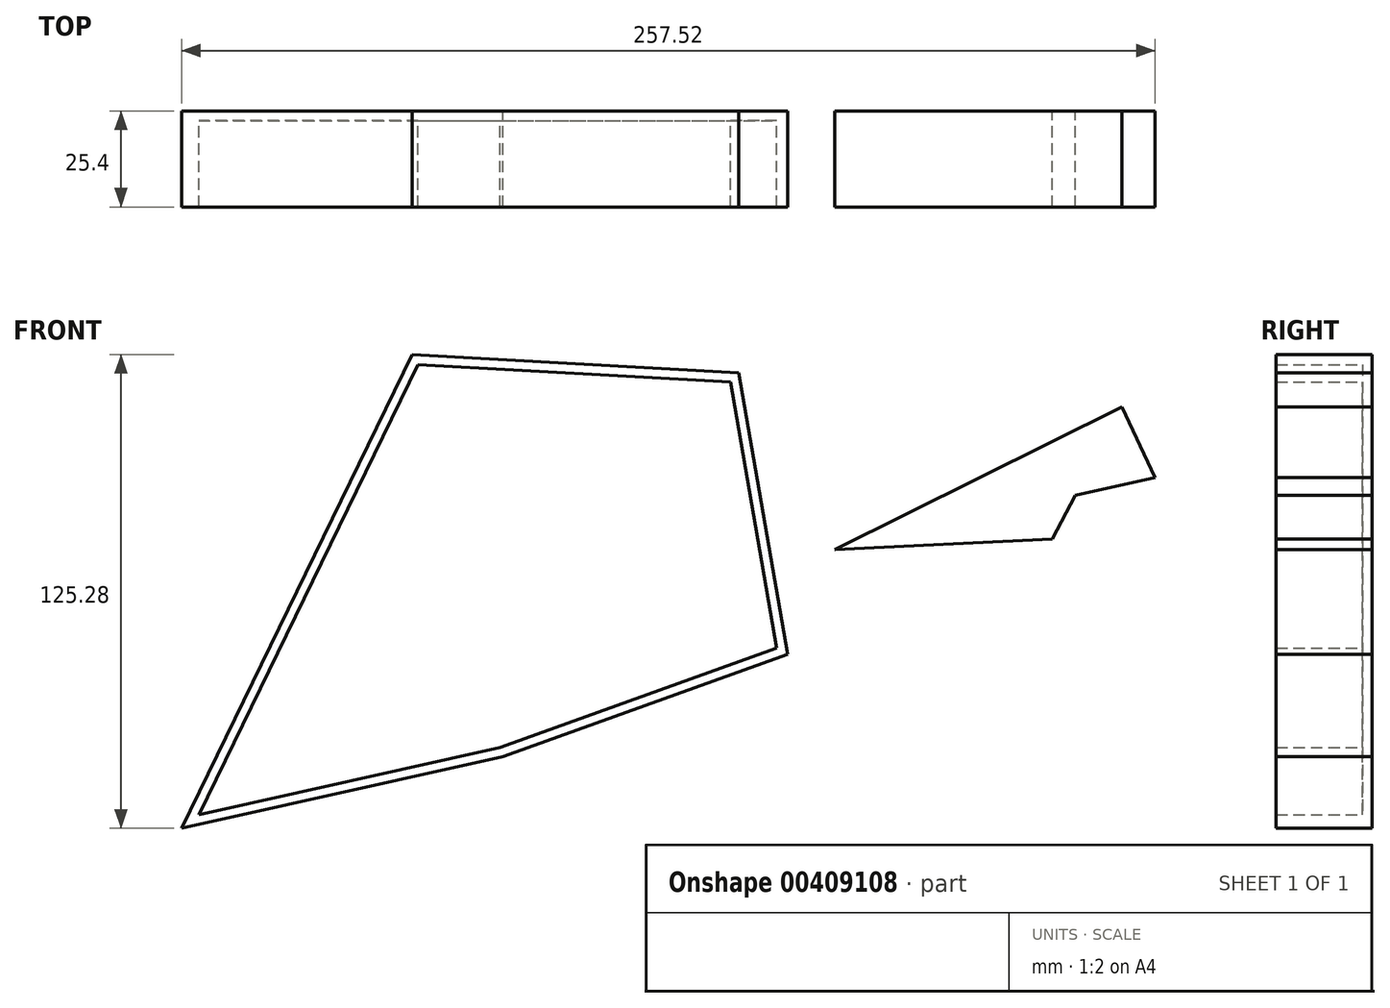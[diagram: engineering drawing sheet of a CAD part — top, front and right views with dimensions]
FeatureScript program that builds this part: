
annotation { "Feature Type Name" : "Feature", "Feature Type Description" : "" }
export const myFeature = defineFeature(function(context is Context, id is Id, definition is map)
    precondition{}
    {
        {
            var Q0;
            Q0=qCreatedBy(makeId("Front.planeOp"),FACE);
            var sketch = newSketch(context, id + "F0", { "sketchPlane" : qUnion([Q0])});
            skLineSegment(sketch, "E0", {"start": v(-59.05, 44.65) * mm, "end": v(27.25, 39.85) * mm});
            skLineSegment(sketch, "E1", {"start": v(27.25, 39.85) * mm, "end": v(-35.04, -61.73) * mm});
            skLineSegment(sketch, "E2", {"start": v(-35.04, -61.73) * mm, "end": v(40.23, -34.58) * mm});
            skLineSegment(sketch, "E3", {"start": v(40.23, -34.58) * mm, "end": v(27.25, 39.85) * mm});
            skLineSegment(sketch, "E4", {"start": v(-59.05, 44.65) * mm, "end": v(-120.05, -80.63) * mm});
            skLineSegment(sketch, "E5", {"start": v(-120.05, -80.63) * mm, "end": v(-47.37, -46.91) * mm});
            skLineSegment(sketch, "E6", {"start": v(-47.37, -46.91) * mm, "end": v(-59.05, 39.85) * mm});
            skLineSegment(sketch, "E7", {"start": v(52.73, -6.92) * mm, "end": v(137.47, 12.14) * mm});
            skLineSegment(sketch, "E8", {"start": v(137.47, 12.14) * mm, "end": v(128.67, 30.8) * mm});
            skLineSegment(sketch, "E9", {"start": v(128.67, 30.8) * mm, "end": v(110.24, -4.15) * mm});
            skLineSegment(sketch, "E10", {"start": v(110.24, -4.15) * mm, "end": v(52.73, -6.92) * mm});
            skLineSegment(sketch, "E11", {"start": v(52.73, -6.92) * mm, "end": v(128.67, 30.8) * mm});
            skLineSegment(sketch, "E12", {"start": v(-120.05, -80.63) * mm, "end": v(-112.6, -77.18) * mm});
            skLineSegment(sketch, "E13", {"start": v(-120.05, -80.63) * mm, "end": v(-35.04, -61.73) * mm});
            skSolve(sketch);
        }
        {
            var Q0;
            Q0 = qSketchRegion(id + "F0", true);
            extrude(context, id + "F1", {"entities" : qUnion([Q0]), "depth" : 25.4 * mm});
        }
        {
            var Q0;
            Q0=makeQuery(id+"F1.opExtrude","CAP_FACE",FACE,{"disambiguationData":[OSD([sQuery(id+"F0.wireOp",EDGE,"E0"),sQuery(id+"F0.wireOp",EDGE,"E2"),sQuery(id+"F0.wireOp",EDGE,"E3"),sQuery(id+"F0.wireOp",EDGE,"E4"),sQuery(id+"F0.wireOp",EDGE,"E13")])],"isStart":false});
            shell(context, id + "F2", {"entities" : qUnion([Q0]), "thickness" : 2.54 * mm});
        }
    });
